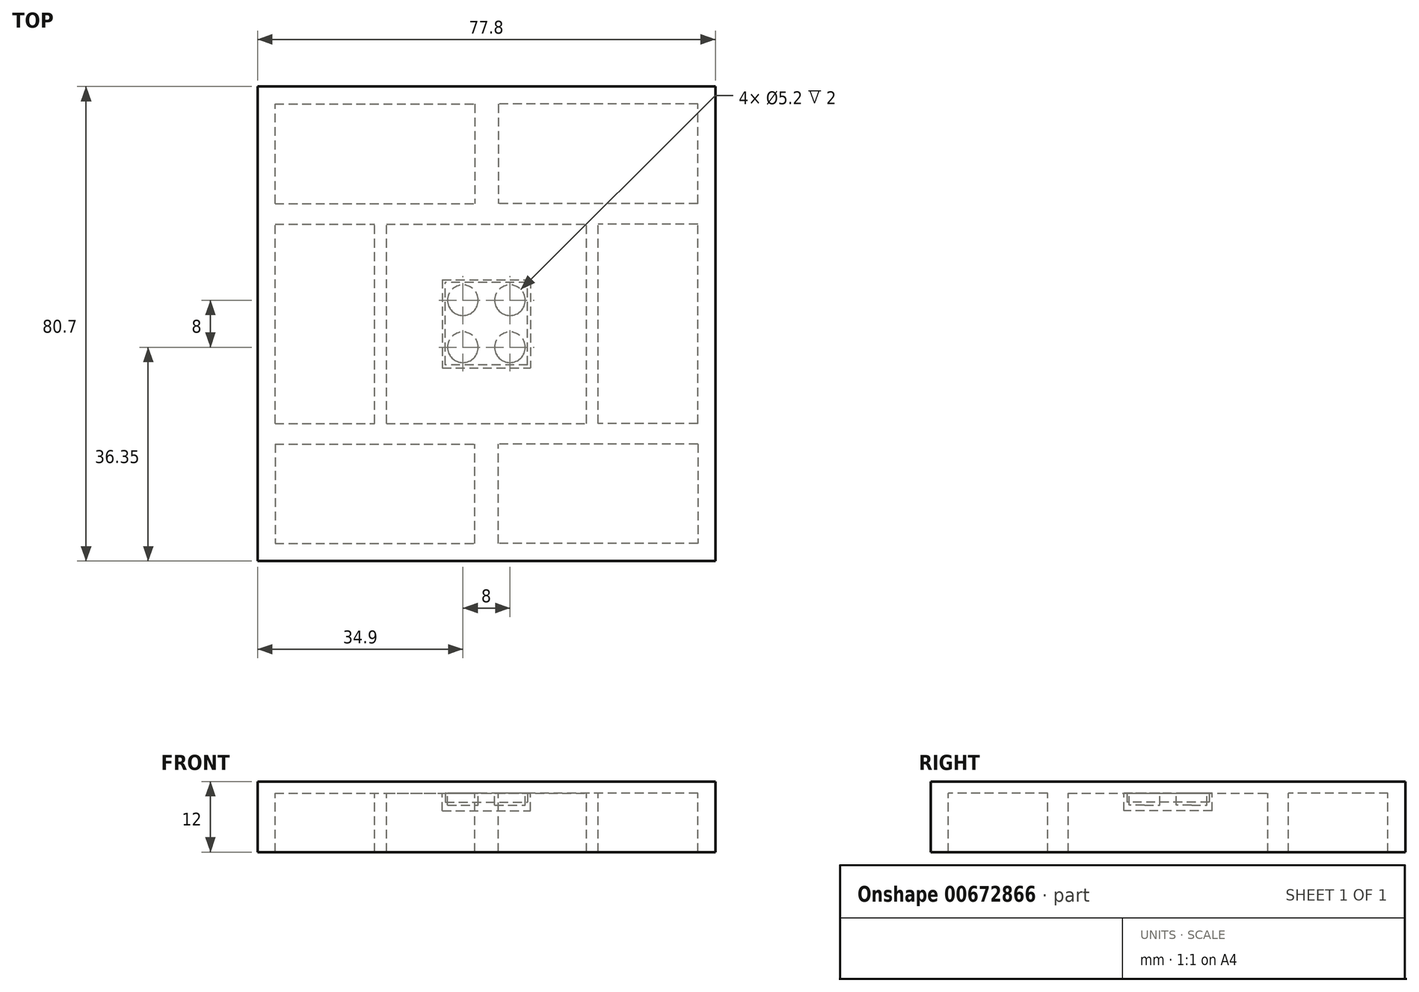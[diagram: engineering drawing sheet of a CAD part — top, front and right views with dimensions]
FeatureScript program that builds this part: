
annotation { "Feature Type Name" : "Feature", "Feature Type Description" : "" }
export const myFeature = defineFeature(function(context is Context, id is Id, definition is map)
    precondition{}
    {
        {
            var Q0;
            Q0=qCreatedBy(makeId("Top.planeOp"),FACE);
            var sketch = newSketch(context, id + "F0", { "sketchPlane" : qUnion([Q0])});
            skLineSegment(sketch, "E0.bottom", {"start": v(-35.9, -16.95) * mm, "end": v(-19, -16.95) * mm});
            skLineSegment(sketch, "E0.top", {"start": v(-35.9, 16.95) * mm, "end": v(-19, 16.95) * mm});
            skLineSegment(sketch, "E0.left", {"start": v(-35.9, -16.95) * mm, "end": v(-35.9, 16.95) * mm});
            skLineSegment(sketch, "E0.right", {"start": v(-19, -16.95) * mm, "end": v(-19, 16.95) * mm});
            skLineSegment(sketch, "E1.bottom", {"start": v(-35.9, -37.35) * mm, "end": v(-2, -37.35) * mm});
            skLineSegment(sketch, "E1.top", {"start": v(-38.9, -20.45) * mm, "end": v(-2, -20.45) * mm});
            skLineSegment(sketch, "E1.left", {"start": v(-38.9, -37.35) * mm, "end": v(-38.9, -20.45) * mm});
            skLineSegment(sketch, "E1.right", {"start": v(-2, -37.35) * mm, "end": v(-2, -20.45) * mm});
            skLineSegment(sketch, "E2.MirrorCS", {"start": v(-35.9, 37.35) * mm, "end": v(-2, 37.35) * mm});
            skLineSegment(sketch, "E3.MirrorCS", {"start": v(-35.9, 20.45) * mm, "end": v(-2, 20.45) * mm});
            skLineSegment(sketch, "E4.MirrorCS", {"start": v(-2, 37.35) * mm, "end": v(-2, 20.45) * mm});
            skLineSegment(sketch, "E5.MirrorCS", {"start": v(-38.9, 37.35) * mm, "end": v(-38.9, 20.45) * mm});
            skLineSegment(sketch, "E6.MirrorCS", {"start": v(2, -37.35) * mm, "end": v(2, -20.45) * mm});
            skLineSegment(sketch, "E7.MirrorCS", {"start": v(38.9, -37.35) * mm, "end": v(38.9, -20.45) * mm});
            skLineSegment(sketch, "E8.MirrorCS", {"start": v(38.9, -20.45) * mm, "end": v(2, -20.45) * mm});
            skLineSegment(sketch, "E9.MirrorCS", {"start": v(35.9, -37.35) * mm, "end": v(2, -37.35) * mm});
            skLineSegment(sketch, "E10.MirrorCS", {"start": v(19, -16.95) * mm, "end": v(19, 16.95) * mm});
            skLineSegment(sketch, "E11.MirrorCS", {"start": v(35.9, -16.95) * mm, "end": v(35.9, 16.95) * mm});
            skLineSegment(sketch, "E12.MirrorCS", {"start": v(35.9, 16.95) * mm, "end": v(19, 16.95) * mm});
            skLineSegment(sketch, "E13.MirrorCS", {"start": v(35.9, -16.95) * mm, "end": v(19, -16.95) * mm});
            skLineSegment(sketch, "E14.MirrorCS", {"start": v(35.9, 37.35) * mm, "end": v(2, 37.35) * mm});
            skLineSegment(sketch, "E15.MirrorCS", {"start": v(35.9, 20.45) * mm, "end": v(2, 20.45) * mm});
            skLineSegment(sketch, "E16.MirrorCS", {"start": v(38.9, 37.35) * mm, "end": v(38.9, 20.45) * mm});
            skLineSegment(sketch, "E17.MirrorCS", {"start": v(2, 37.35) * mm, "end": v(2, 20.45) * mm});
            skLineSegment(sketch, "E18", {"start": v(-38.9, -37.35) * mm, "end": v(-38.9, -40.35) * mm});
            skLineSegment(sketch, "E19", {"start": v(-38.9, -40.35) * mm, "end": v(38.9, -40.35) * mm});
            skLineSegment(sketch, "E20", {"start": v(38.9, -40.35) * mm, "end": v(38.9, -37.35) * mm});
            skLineSegment(sketch, "E21.MirrorCS", {"start": v(38.9, 40.35) * mm, "end": v(38.9, 37.35) * mm});
            skLineSegment(sketch, "E22.MirrorCS", {"start": v(-38.9, 37.35) * mm, "end": v(-38.9, 40.35) * mm});
            skLineSegment(sketch, "E23.MirrorCS", {"start": v(-38.9, 40.35) * mm, "end": v(38.9, 40.35) * mm});
            skLineSegment(sketch, "E24", {"start": v(-38.9, -20.45) * mm, "end": v(-38.9, 20.45) * mm});
            skLineSegment(sketch, "E25", {"start": v(38.9, -20.45) * mm, "end": v(38.9, 20.45) * mm});
            skLineSegment(sketch, "E26.bottom", {"start": v(-17, -16.95) * mm, "end": v(17, -16.95) * mm});
            skLineSegment(sketch, "E26.top", {"start": v(-17, 16.95) * mm, "end": v(17, 16.95) * mm});
            skLineSegment(sketch, "E26.left", {"start": v(-17, -16.95) * mm, "end": v(-17, 16.95) * mm});
            skLineSegment(sketch, "E26.right", {"start": v(17, -16.95) * mm, "end": v(17, 16.95) * mm});
            skLineSegment(sketch, "E27", {"start": v(-35.9, -20.45) * mm, "end": v(-35.9, -37.35) * mm});
            skLineSegment(sketch, "E28", {"start": v(35.9, -20.45) * mm, "end": v(35.9, -37.35) * mm});
            skLineSegment(sketch, "E29", {"start": v(35.9, 20.45) * mm, "end": v(35.9, 37.35) * mm});
            skLineSegment(sketch, "E30", {"start": v(-35.9, 20.45) * mm, "end": v(-35.9, 37.35) * mm});
            skSolve(sketch);
        }
        {
            var Q0;
            Q0 = qSketchRegion(id + "F0", true);
            extrude(context, id + "F1", {"entities" : qUnion([Q0]), "oppositeDirection" : true, "depth" : 10 * mm, "offsetDistance" : 25 * mm});
        }
        {
            var Q0;
            Q0=qCreatedBy(makeId("Top.planeOp"),FACE);
            var sketch = newSketch(context, id + "F2", { "sketchPlane" : qUnion([Q0])});
            skLineSegment(sketch, "E31.bottom", {"start": v(-38.9, 40.35) * mm, "end": v(38.9, 40.35) * mm});
            skLineSegment(sketch, "E31.top", {"start": v(-38.9, -40.35) * mm, "end": v(38.9, -40.35) * mm});
            skLineSegment(sketch, "E31.left", {"start": v(-38.9, 40.35) * mm, "end": v(-38.9, -40.35) * mm});
            skLineSegment(sketch, "E31.right", {"start": v(38.9, 40.35) * mm, "end": v(38.9, -40.35) * mm});
            skSolve(sketch);
        }
        {
            var Q0;
            Q0 = qSketchRegion(id + "F2", true);
            extrude(context, id + "F3", {"entities" : qUnion([Q0]), "operationType" : NewBodyOperationType.ADD, "depth" : 2 * mm, "offsetDistance" : 25 * mm});
        }
        {
            var Q0;
            Q0=qCreatedBy(makeId("Top.planeOp"),FACE);
            var sketch = newSketch(context, id + "F4", { "sketchPlane" : qUnion([Q0])});
            skLineSegment(sketch, "E32.bottom", {"start": v(-7, 7) * mm, "end": v(7, 7) * mm});
            skLineSegment(sketch, "E32.top", {"start": v(-7, -7) * mm, "end": v(7, -7) * mm});
            skLineSegment(sketch, "E32.left", {"start": v(-7, 7) * mm, "end": v(-7, -7) * mm});
            skLineSegment(sketch, "E32.right", {"start": v(7, 7) * mm, "end": v(7, -7) * mm});
            skCircle(sketch, "E33", {"center": v(-4, 4) * mm, "radius": 2.43 * mm});
            skCircle(sketch, "E34.MirrorC", {"center": v(-4, -4) * mm, "radius": 2.43 * mm});
            skCircle(sketch, "E35.MirrorC", {"center": v(4, -4) * mm, "radius": 2.43 * mm});
            skCircle(sketch, "E36.MirrorC", {"center": v(4, 4) * mm, "radius": 2.43 * mm});
            skSolve(sketch);
        }
        {
            var Q0;
            Q0=makeQuery(id+"F4.imprint","IMPRINT",FACE,{"disambiguationData":[TD([[makeQuery(id+"F4.imprint","IMPRINT",EDGE,{"derivedFrom":sQuery(id+"F4.wireOp",EDGE,"E33")}),1.0]])]});
            var Q1;
            Q1=makeQuery(id+"F4.imprint","IMPRINT",FACE,{"disambiguationData":[TD([[makeQuery(id+"F4.imprint","IMPRINT",EDGE,{"derivedFrom":sQuery(id+"F4.wireOp",EDGE,"E36.MirrorC")}),-1.0]])]});
            var Q2;
            Q2=makeQuery(id+"F4.imprint","IMPRINT",FACE,{"disambiguationData":[TD([[makeQuery(id+"F4.imprint","IMPRINT",EDGE,{"derivedFrom":sQuery(id+"F4.wireOp",EDGE,"E34.MirrorC")}),-1.0]])]});
            var Q3;
            Q3=makeQuery(id+"F4.imprint","IMPRINT",FACE,{"disambiguationData":[TD([[makeQuery(id+"F4.imprint","IMPRINT",EDGE,{"derivedFrom":sQuery(id+"F4.wireOp",EDGE,"E35.MirrorC")}),1.0]])]});
            extrude(context, id + "F5", {"entities" : qUnion([Q0, Q1, Q2, Q3]), "depth" : 1.6 * mm, "offsetDistance" : 25 * mm});
        }
        {
            var Q0;
            Q0=qCreatedBy(makeId("Top.planeOp"),FACE);
            var sketch = newSketch(context, id + "F6", { "sketchPlane" : qUnion([Q0])});
            skLineSegment(sketch, "E37.bottom", {"start": v(-7, -7) * mm, "end": v(7, -7) * mm});
            skLineSegment(sketch, "E37.top", {"start": v(-7, 7) * mm, "end": v(7, 7) * mm});
            skLineSegment(sketch, "E37.left", {"start": v(-7, 7) * mm, "end": v(-7, -7) * mm});
            skLineSegment(sketch, "E37.right", {"start": v(7, 7) * mm, "end": v(7, -7) * mm});
            skSolve(sketch);
        }
        {
            var Q0;
            Q0 = qSketchRegion(id + "F6", true);
            extrude(context, id + "F7", {"entities" : qUnion([Q0]), "operationType" : NewBodyOperationType.ADD, "oppositeDirection" : true, "depth" : 1.5 * mm, "offsetDistance" : 25 * mm});
        }
        {
            var Q0;
            Q0=qCreatedBy(makeId("Top.planeOp"),FACE);
            var sketch = newSketch(context, id + "F8", { "sketchPlane" : qUnion([Q0])});
            skLineSegment(sketch, "E38.bottom", {"start": v(-7.5, 7.5) * mm, "end": v(7.5, 7.5) * mm});
            skLineSegment(sketch, "E38.top", {"start": v(-7.5, -7.5) * mm, "end": v(7.5, -7.5) * mm});
            skLineSegment(sketch, "E38.left", {"start": v(-7.5, 7.5) * mm, "end": v(-7.5, -7.5) * mm});
            skLineSegment(sketch, "E38.right", {"start": v(7.5, 7.5) * mm, "end": v(7.5, -7.5) * mm});
            skCircle(sketch, "E39", {"center": v(-4, 4) * mm, "radius": 2.6 * mm});
            skCircle(sketch, "E40.MirrorC", {"center": v(4, 4) * mm, "radius": 2.6 * mm});
            skCircle(sketch, "E41.MirrorC", {"center": v(-4, -4) * mm, "radius": 2.6 * mm});
            skCircle(sketch, "E42.MirrorC", {"center": v(4, -4) * mm, "radius": 2.6 * mm});
            skSolve(sketch);
        }
        {
            var Q0;
            Q0 = qSketchRegion(id + "F8", true);
            extrude(context, id + "F9", {"entities" : qUnion([Q0]), "oppositeDirection" : true, "depth" : 3 * mm, "offsetDistance" : 25 * mm});
        }
        {
            var Q0;
            Q0=makeQuery(id+"F9.opExtrude","CAP_FACE",FACE,{"disambiguationData":[OSD([sQuery(id+"F8.wireOp",EDGE,"E38.bottom"),sQuery(id+"F8.wireOp",EDGE,"E38.top"),sQuery(id+"F8.wireOp",EDGE,"E38.left"),sQuery(id+"F8.wireOp",EDGE,"E38.right"),sQuery(id+"F8.wireOp",EDGE,"E39"),sQuery(id+"F8.wireOp",EDGE,"E40.MirrorC"),sQuery(id+"F8.wireOp",EDGE,"E41.MirrorC"),sQuery(id+"F8.wireOp",EDGE,"E42.MirrorC")])],"isStart":false});
            var sketch = newSketch(context, id + "F10", { "sketchPlane" : qUnion([Q0])});
            skLineSegment(sketch, "E43.bottom", {"start": v(-7.5, 7.5) * mm, "end": v(7.5, 7.5) * mm});
            skLineSegment(sketch, "E43.top", {"start": v(-7.5, -7.5) * mm, "end": v(7.5, -7.5) * mm});
            skLineSegment(sketch, "E43.left", {"start": v(-7.5, 7.5) * mm, "end": v(-7.5, -7.5) * mm});
            skLineSegment(sketch, "E43.right", {"start": v(7.5, 7.5) * mm, "end": v(7.5, -7.5) * mm});
            skSolve(sketch);
        }
        {
            var Q0;
            Q0 = qSketchRegion(id + "F10", true);
            extrude(context, id + "F11", {"entities" : qUnion([Q0]), "operationType" : NewBodyOperationType.ADD, "oppositeDirection" : true, "depth" : 1 * mm, "offsetDistance" : 25 * mm});
        }
    });
